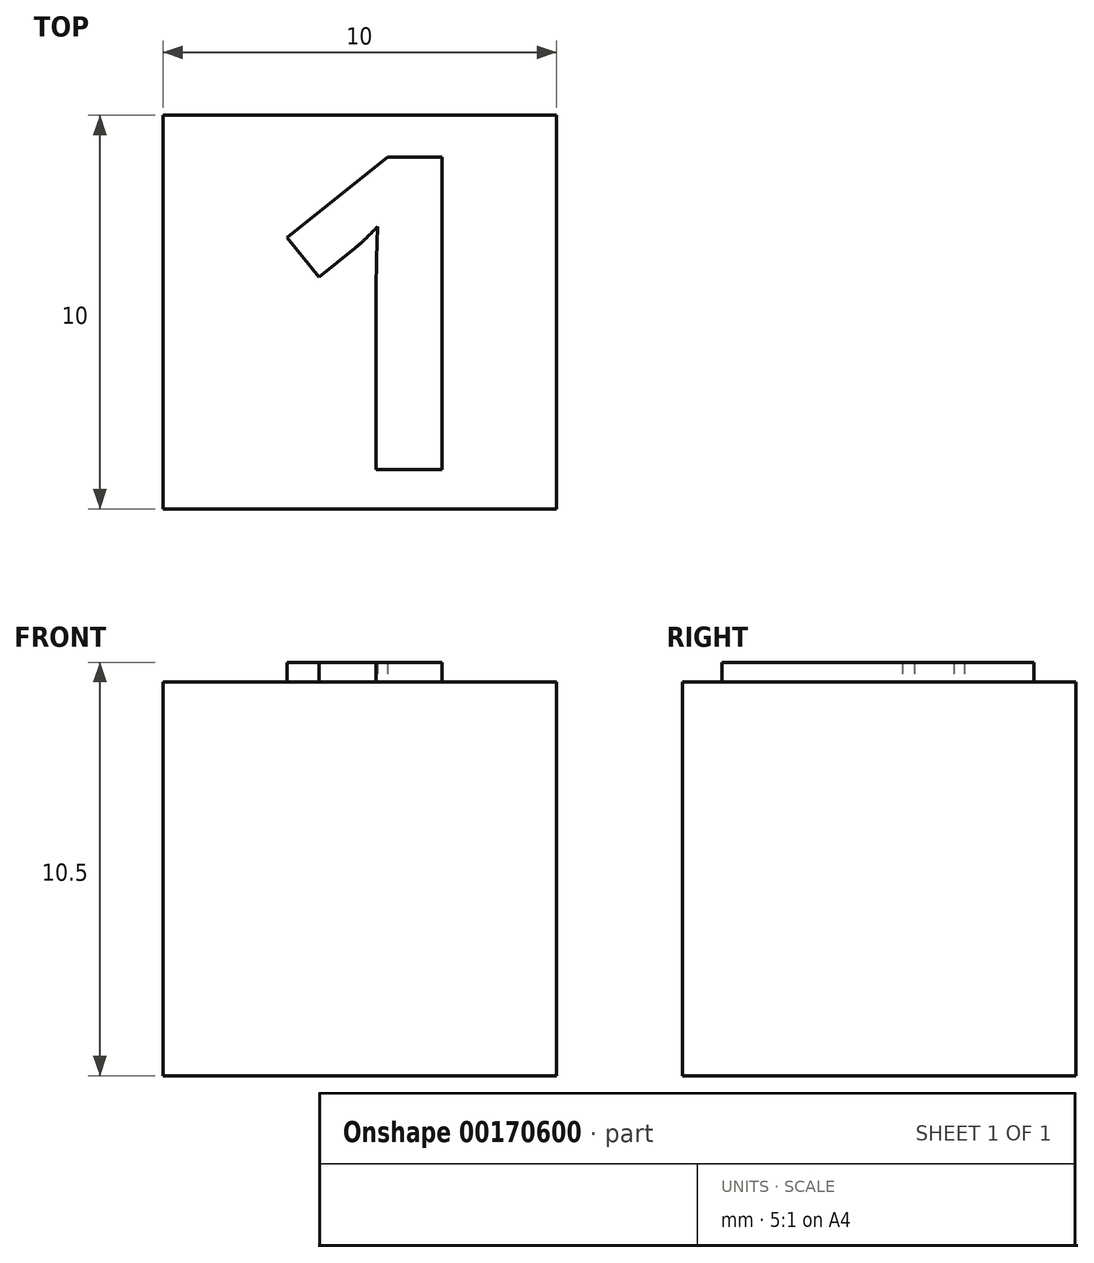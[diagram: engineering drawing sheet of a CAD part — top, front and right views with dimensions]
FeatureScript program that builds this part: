
annotation { "Feature Type Name" : "Feature", "Feature Type Description" : "" }
export const myFeature = defineFeature(function(context is Context, id is Id, definition is map)
    precondition{}
    {
        {
            var Q0;
            Q0=qCreatedBy(makeId("Top.planeOp"),FACE);
            var sketch = newSketch(context, id + "F0", { "sketchPlane" : qUnion([Q0])});
            skLineSegment(sketch, "E0.bottom", {"start": v(0, 0) * mm, "end": v(10, 0) * mm});
            skLineSegment(sketch, "E0.top", {"start": v(0, 10) * mm, "end": v(10, 10) * mm});
            skLineSegment(sketch, "E0.left", {"start": v(0, 0) * mm, "end": v(0, 10) * mm});
            skLineSegment(sketch, "E0.right", {"start": v(10, 0) * mm, "end": v(10, 10) * mm});
            skSolve(sketch);
        }
        {
            var Q0;
            Q0=makeQuery(id+"F0.imprint","IMPRINT",FACE,{"disambiguationData":[TD([[makeQuery(id+"F0.imprint","IMPRINT",EDGE,{"derivedFrom":sQuery(id+"F0.wireOp",EDGE,"E0.bottom")}),1.0]])]});
            extrude(context, id + "F1", {"entities" : qUnion([Q0]), "depth" : 10 * mm});
        }
        {
            var Q0;
            Q0=makeQuery(id+"F1.opExtrude","CAP_FACE",FACE,{"disambiguationData":[OSD([sQuery(id+"F0.wireOp",EDGE,"E0.bottom"),sQuery(id+"F0.wireOp",EDGE,"E0.top"),sQuery(id+"F0.wireOp",EDGE,"E0.left"),sQuery(id+"F0.wireOp",EDGE,"E0.right")])],"isStart":false});
            var sketch = newSketch(context, id + "F2", { "sketchPlane" : qUnion([Q0])});
            skText(sketch, "E1", { "text": "1", "fontName": "OpenSans-Bold.ttf"});
            const initialGuessF2  = {"E1": [0.0025, 0.001, 1, 0, 0.008]};
            skSetInitialGuess(sketch, initialGuessF2);
            skSolve(sketch);
        }
        {
            var Q0;
            Q0 = qSketchRegion(id + "F2", true);
            extrude(context, id + "F3", {"entities" : qUnion([Q0]), "operationType" : NewBodyOperationType.ADD, "depth" : 0.5 * mm});
        }
    });
